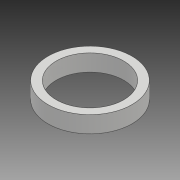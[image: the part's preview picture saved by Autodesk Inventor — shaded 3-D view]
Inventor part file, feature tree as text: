
AUTODESK INVENTOR PART (.ipt)
format: ipt  version: 2018 (Build 220112000, 112)  size: 82,432 bytes
history: native  units: mm
features: other x1, extrude x1, sketch x1
ambient origin geometry x8: Origin, YZ Plane, XZ Plane, XY Plane, X Axis, Y Axis, Z Axis, Center Point
bodies: Body1 (feature_tree)
feature tree (3):
  other  "ソリッド1"
  extrude  "押し出し1"  Depth=5.0mm
  sketch  "スケッチ1"
